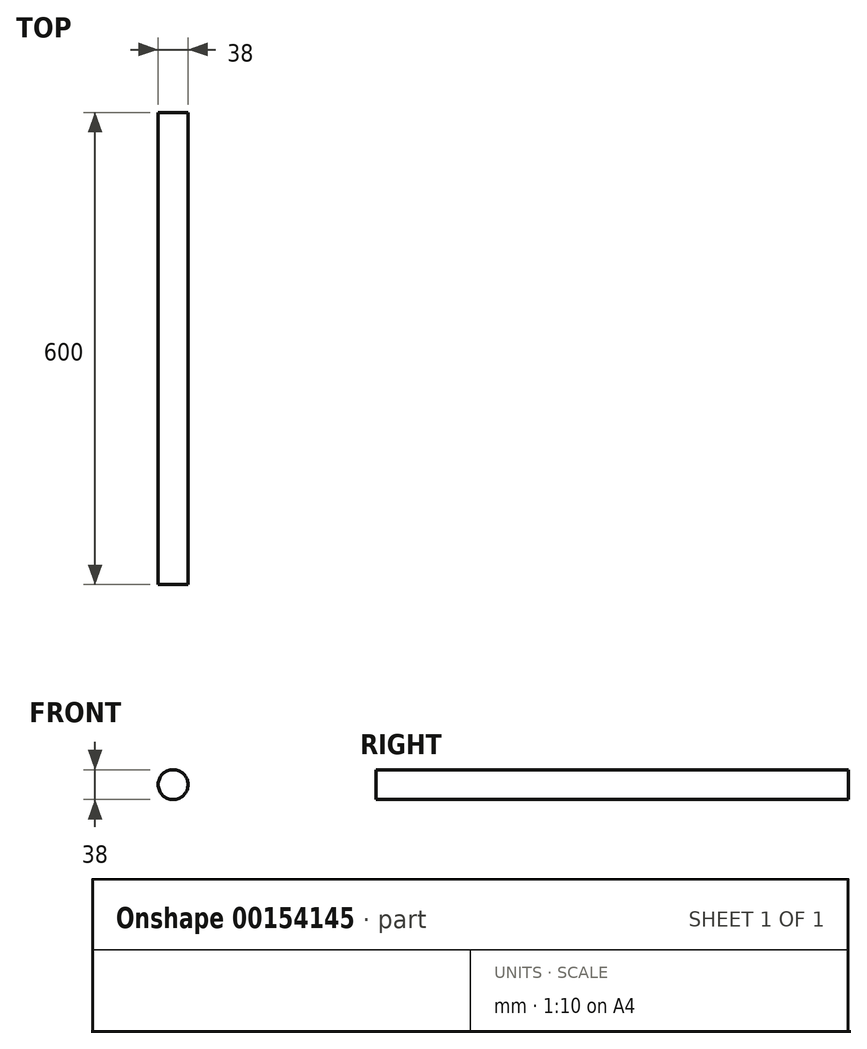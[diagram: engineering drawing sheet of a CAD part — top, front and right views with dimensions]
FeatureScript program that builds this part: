
annotation { "Feature Type Name" : "Feature", "Feature Type Description" : "" }
export const myFeature = defineFeature(function(context is Context, id is Id, definition is map)
    precondition{}
    {
        {
            var Q0;
            Q0=qCreatedBy(makeId("Front.planeOp"),FACE);
            var sketch = newSketch(context, id + "F0", { "sketchPlane" : qUnion([Q0])});
            skCircle(sketch, "E0", {"center": v(0, 0) * mm, "radius": 19 * mm});
            skSolve(sketch);
        }
        {
            var Q0;
            Q0 = qSketchRegion(id + "F0", true);
            extrude(context, id + "F1", {"entities" : qUnion([Q0]), "depth" : 600 * mm, "offsetDistance" : 25 * mm});
        }
    });
